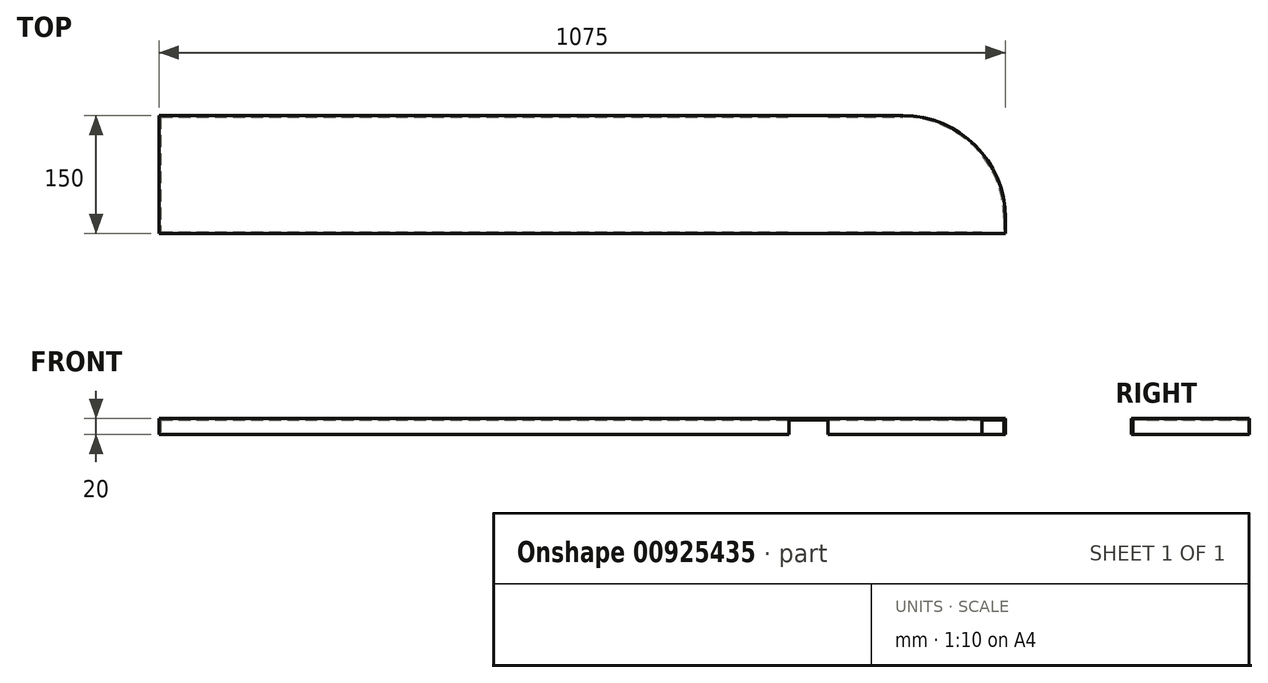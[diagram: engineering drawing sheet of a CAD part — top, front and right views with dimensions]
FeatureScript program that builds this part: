
annotation { "Feature Type Name" : "Feature", "Feature Type Description" : "" }
export const myFeature = defineFeature(function(context is Context, id is Id, definition is map)
    precondition{}
    {
        {
            var Q0;
            Q0=qCreatedBy(makeId("Top.planeOp"),FACE);
            var sketch = newSketch(context, id + "F0", { "sketchPlane" : qUnion([Q0])});
            skLineSegment(sketch, "E0.bottom", {"start": v(0, 0) * mm, "end": v(945, 0) * mm});
            skLineSegment(sketch, "E0.top", {"start": v(0, -150) * mm, "end": v(1075, -150) * mm});
            skLineSegment(sketch, "E0.left", {"start": v(0, 0) * mm, "end": v(0, -150) * mm});
            skLineSegment(sketch, "E0.right", {"start": v(1075, -130) * mm, "end": v(1075, -150) * mm});
            skPoint(sketch, "E1.visualSharp", {"position": v(1075, 0) * mm});
            skArc(sketch, "E1.filletArc", {"start": v(1075, -130) * mm, "mid": v(1036.92, -38.08) * mm, "end": v(945, 0) * mm});
            skSolve(sketch);
        }
        {
            var Q0;
            Q0 = qSketchRegion(id + "F0", true);
            extrude(context, id + "F1", {"entities" : qUnion([Q0]), "depth" : 20 * mm, "offsetDistance" : 25 * mm});
        }
        {
            var Q0;
            Q0=makeQuery(id+"F1.opExtrude","CAP_FACE",FACE,{"disambiguationData":[OSD([sQuery(id+"F0.wireOp",EDGE,"E0.bottom"),sQuery(id+"F0.wireOp",EDGE,"E0.top"),sQuery(id+"F0.wireOp",EDGE,"E0.left"),sQuery(id+"F0.wireOp",EDGE,"E0.right"),sQuery(id+"F0.wireOp",EDGE,"E1.filletArc")])],"isStart":true});
            shell(context, id + "F2", {"entities" : qUnion([Q0]), "thickness" : 2 * mm});
        }
        {
            var Q0;
            Q0=makeQuery(id+"F1.opExtrude","SWEPT_FACE",FACE,{"disambiguationData":[OSD([sQuery(id+"F0.wireOp",EDGE,"E0.top")])]});
            var sketch = newSketch(context, id + "F3", { "sketchPlane" : qUnion([Q0])});
            skLineSegment(sketch, "E2.bottom", {"start": v(800, 0) * mm, "end": v(850, 0) * mm});
            skLineSegment(sketch, "E2.top", {"start": v(800, 18) * mm, "end": v(850, 18) * mm});
            skLineSegment(sketch, "E2.left", {"start": v(800, 0) * mm, "end": v(800, 18) * mm});
            skLineSegment(sketch, "E2.right", {"start": v(850, 0) * mm, "end": v(850, 18) * mm});
            skSolve(sketch);
        }
        {
            var Q0;
            Q0 = qSketchRegion(id + "F3", true);
            extrude(context, id + "F4", {"entities" : qUnion([Q0]), "operationType" : NewBodyOperationType.REMOVE, "oppositeDirection" : true, "depth" : 600 * mm, "offsetDistance" : 25 * mm});
        }
        {
            var Q0;
            Q0=makeQuery(id+"F1.opExtrude","SWEPT_FACE",FACE,{"disambiguationData":[OSD([sQuery(id+"F0.wireOp",EDGE,"E0.top")])]});
            var sketch = newSketch(context, id + "F5", { "sketchPlane" : qUnion([Q0])});
            skLineSegment(sketch, "E3.bottom", {"start": v(1075, 0) * mm, "end": v(1045, 0) * mm});
            skLineSegment(sketch, "E3.top", {"start": v(1075, 18) * mm, "end": v(1045, 18) * mm});
            skLineSegment(sketch, "E3.left", {"start": v(1075, 0) * mm, "end": v(1075, 18) * mm});
            skLineSegment(sketch, "E3.right", {"start": v(1045, 0) * mm, "end": v(1045, 18) * mm});
            skSolve(sketch);
        }
        {
            var Q0;
            Q0 = qSketchRegion(id + "F5", true);
            extrude(context, id + "F6", {"entities" : qUnion([Q0]), "operationType" : NewBodyOperationType.REMOVE, "oppositeDirection" : true, "depth" : 2 * mm, "offsetDistance" : 25 * mm});
        }
    });
